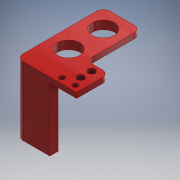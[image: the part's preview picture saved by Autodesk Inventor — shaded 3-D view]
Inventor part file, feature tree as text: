
AUTODESK INVENTOR PART (.ipt)
format: ipt  version: 2018.3 (Build 223284000, 284)  size: 372,736 bytes
history: native  units: mm
features: extrude x13, sketch x13, fillet x9, chamfer x2
ambient origin geometry x8: Origin, YZ Plane, XZ Plane, XY Plane, X Axis, Y Axis, Z Axis, Center Point
bodies: Solid1 (feature_tree)
feature tree (37):
  extrude  "Extrusion1"  Depth=4.0mm
  sketch  "Sketch2"  dims[d4=16.5mm d5=16.5mm]
  fillet  "Fillet3"  Radius=4.0mm
  extrude  "Extrusion5"  Depth=16.5mm
  extrude  "Extrusion8"  Depth=14.0mm
  fillet  "Fillet4"  Radius=25.883mm
  extrude  "Extrusion9"  Depth=4.0mm
  extrude  "Extrusion10"  Depth=4.0mm
  fillet  "Fillet6"  Radius=10.0mm
  extrude  "Extrusion11"  Depth=4.0mm
  extrude  "Extrusion12"  Depth=22.0mm
  extrude  "Extrusion14"  Depth=1.0mm
  extrude  "Extrusion15"  Depth=3.0mm
  extrude  "Extrusion16"  Depth=3.0mm TaperAngle=0.0deg
  chamfer  "Chamfer1"  Distance=5.0mm
  extrude  "Extrusion17"  Depth=2.0mm
  fillet  "Fillet9"  Radius=8.1mm
  extrude  "Extrusion18"  Depth=10.0mm TaperAngle=0.0deg
  extrude  "Extrusion19"  Depth=2.0mm
  fillet  "Fillet10"  Radius=3.0mm
  fillet  "Fillet11"  Radius=48.0mm
  fillet  "Fillet12"  Radius=1.5mm
  fillet  "Fillet13"  Radius=30.0mm
  fillet  "Fillet14"  Radius=3.925mm
  chamfer  "Chamfer2"  Distance=12.2915mm
  sketch  "Sketch1"  dims[d0=45.0mm d1=65.0mm d2=4.0mm d3=0.0mm]
  sketch  "Sketch4"  dims[d6=14.0mm d7=14.0mm d8=25.883mm]
  sketch  "Sketch6"  dims[d19=5.0mm d20=4.0mm]
  sketch  "Sketch7"  dims[d21=5.0mm d22=4.0mm d24=10.0mm]
  sketch  "Sketch8"  dims[d25=0.0mm d26=0.0mm d27=4.0mm]
  sketch  "Sketch9"  dims[d34=22.0mm d35=22.0mm]
  sketch  "Sketch10"  dims[d36=3.0mm d37=0.0mm d38=1.0mm]
  sketch  "Sketch11"  dims[d39=3.0mm d40=0.0mm d41=20.2mm]
  sketch  "Sketch12"  dims[d42=14.0mm d43=3.0mm d44=0.0mm]
  sketch  "Sketch13"  dims[d46=5.0mm]
  sketch  "Sketch14"  dims[d47=5.4mm]
  sketch  "Sketch15"  dims[d48=8.1mm d49=5.0mm d50=5.4mm d51=8.1mm d52=10.0mm d53=0.0mm d54=20.0mm d55=3.0mm d56=48.0mm d57=0.0mm d62=1.5mm d63=30.0mm d65=3.925mm d66=12.2915mm d67=10.0mm d68=90.0deg d71=10.0mm d72=15.0mm d73=3.0mm d74=1.0mm d75=1.0mm d76=0.0mm d77=7.5mm d78=4.0mm d79=0.0mm d80=3.0mm d81=2.5mm d82=2.5mm d83=4.0mm d84=0.0mm d85=2.5mm d86=4.0mm d87=45.0deg d88=5.0mm d89=1.5mm d90=4.0mm d91=5.0mm d92=1.5mm d93=3.0mm d94=3.0mm d95=0.0mm d98=1.5mm d99=2.0mm d100=0.0mm d101=2.0mm d102=2.0mm d103=90.0deg d104=2.0mm d105=0.0mm d106=0.5mm d107=0.5mm d108=1.0mm d109=1.0mm d110=1.0mm d111=1.0mm d112=2.0mm d113=45.0deg]
